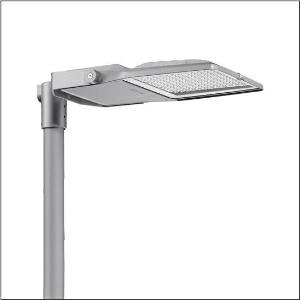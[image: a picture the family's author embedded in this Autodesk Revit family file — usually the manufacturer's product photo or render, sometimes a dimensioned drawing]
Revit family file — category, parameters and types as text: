
# Revit family: floodlight_fl_21_iq_midi___pl64_5xa7781f2e3a_9caf
name_source: partatom
category: Lighting Fixtures
units: mm (PartAtom-declared; Revit-internal decimal feet)

## family parameters
Cut with Voids When Loaded = No
Host = Face
Light Source = No
Part Type = Normal
Room Calculation Point = No
Round Connector Dimension = Use Diameter
Shared = No

## types (1)
- --- (1 x LED, 34530 lm, 270.2 W, 3000K)
    Apparent Load = 270 VA
    CIE Flux Codes = 28 80 98 100 100
    Color Rendering = 70
    Color Temperature = 3000K
    Default Elevation = 1800 mm
    Description = Floodlight FL 21 iQ midi, floodlight, primary light control with lens, of PMMA, primary optical cover: protective disc, of toughened safety glass, transparent, light distribution: PL64, light emission: direct distribution, installation type: surface-mounted, lamps: LED, High Power LED, rated values: 34.530lm | 270,2W | 127,8lm/W (begin service life); end service life: 34.530lm | 286,6W; at 50% lumin. flux: 17.265lm | 117,4W | 147,1lm/W, colour temperature: 3000K, colour rendering: CRI > 70, light colour: 730, light setting 1 begin service life: 100% | 34.530lm | 270,2W | 127,8lm/W | 3.000K, light setting 1 end service life: 286,6W, further light settings possible, control: optimised constant luminous flux control (CLO 2.0), Desk-Remote (wireless, voltage-free reading and setting of iQ features in the workshop via application-optimized NFC function/RFID function), Light-Fading, Smart-Wire, Night-Set, Lumen-Switch, Temp-Guard, Auto-Match, pre-setting: linear dimming characteristic, with terminal, 6-pole, mains connection: 220..240V, AC, 50/60Hz, luminaire housing, of diecast aluminium, powder-coated, SITECO metallic grey (DB 702S), corrosivity category C5 mid according to DIN EN ISO 12944suitable for swimming poolschlorine-resistant, sealing non-destructively replaceable, please order mast flange separately, mast bracket, of steel, galvanised, powder-coated, SITECO metallic grey (DB 702S), protection rating (complete): IP66, insulation class (complete): insulation class II (safety insulation), certification: CE, ENEC, VDE, protection symbol: D, impact resistance: IK08, permissible operating ambient temperature: -40..+40°C, permissible operating ambient temperature for outdoor applications: -40..+50°C, standard: DIN EN 12944, LABS conformity tested according to VDMA 24364:2018-05, packaging unit: 1 piece

Light Distribution: PL64
    Height = 76 mm
    Lamp = 1 x LED
    Lamp Light Flux = 34530 lm
    Lamp Power = 270.2 W
    Lamp count = 1
    Length = 657 mm
    Luminous efficacy = 128 lm/W
    Manufacturer = Siteco
    ModVariant = No
    Model = 5XA7781F2E3A
    Mounting Place = Pole
    Mounting Type = Pole annexe
    Number of Poles = 1
    OnlyDefault = Yes
    Power Factor = 1
    Product Name = Floodlight FL 21 iQ midi | PL64
    Product group = floodlight | pylon annexe
    ProductGroupID = 6201
    Protection Class = Protection class II
    Protection Degree = IP 66
    RLX_Detail_Level = 1
    RLX_Emergency_Light_Flux = 0 lm
    RLX_Emergency_Type = 0
    RLX_Emergency_Type_DB = No
    RlxData = <blob elided: 153721 chars, md5=f3ec19d6>
    Socket = socket
    Standby Power = 0 W
    System Light Flux = 34530 lm
    System Power = 270 W
    Type Comments = factory setting: luminous flux: 100 % | dim-lin: 254 | 620 mA
    Type Image = l_1007123.jpg
    URL = http://relux.com
    VarID = @adj_108369
    Voltage = 0 V
    Weight = 0.00 kg
    Width = 442 mm

## geometry (parser evidence)
native form markers: Blend x4, Sweep x12
no freeform markers — native parametric forms only
